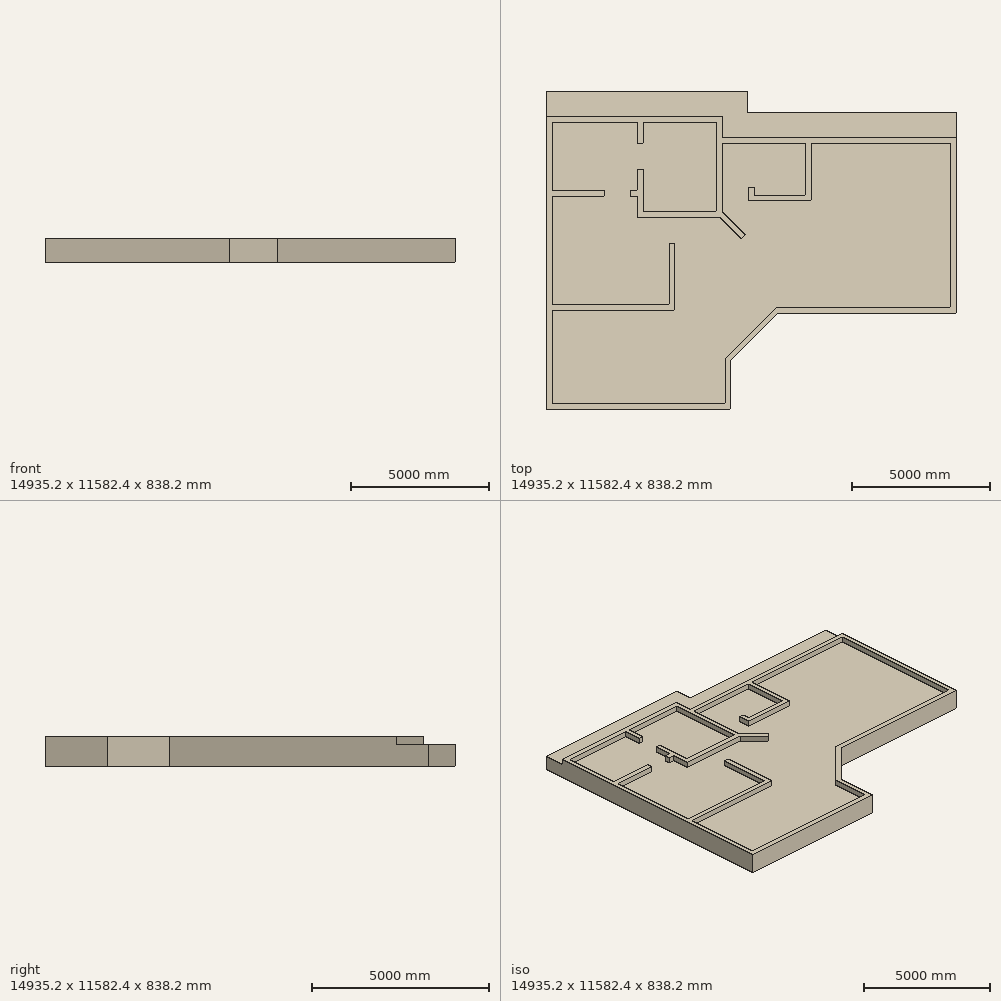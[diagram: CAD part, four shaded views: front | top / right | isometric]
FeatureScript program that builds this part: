
annotation { "Feature Type Name" : "Feature", "Feature Type Description" : "" }
export const myFeature = defineFeature(function(context is Context, id is Id, definition is map)
    precondition{}
    {
        {
            var Q0;
            Q0=qCreatedBy(makeId("Top.planeOp"),FACE);
            var sketch = newSketch(context, id + "F0", { "sketchPlane" : qUnion([Q0])});
            skLineSegment(sketch, "E0.bottom", {"start": v(0, 0) * mm, "end": v(14935.2, 0) * mm});
            skLineSegment(sketch, "E0.top", {"start": v(0, 11582.4) * mm, "end": v(7315.2, 11582.4) * mm});
            skLineSegment(sketch, "E0.left", {"start": v(0, 0) * mm, "end": v(0, 11582.4) * mm});
            skLineSegment(sketch, "E0.right", {"start": v(14935.2, 0) * mm, "end": v(14935.2, 10820.4) * mm});
            skLineSegment(sketch, "E1", {"start": v(14935.2, 10820.4) * mm, "end": v(7315.2, 10820.4) * mm});
            skLineSegment(sketch, "E2", {"start": v(7315.2, 10820.4) * mm, "end": v(7315.2, 11582.4) * mm});
            skLineSegment(sketch, "E3", {"start": v(6705.6, 0) * mm, "end": v(6705.6, 3505.2) * mm});
            skLineSegment(sketch, "E4", {"start": v(6705.6, 3505.2) * mm, "end": v(14935.2, 3505.2) * mm});
            skLineSegment(sketch, "E5", {"start": v(6705.6, 1752.6) * mm, "end": v(8458.2, 3505.2) * mm});
            skLineSegment(sketch, "E6", {"start": v(6705.6, 1752.6) * mm, "end": v(14935.2, 1752.6) * mm, "construction": true});
            skSolve(sketch);
        }
        {
            var Q0;
            Q0=makeQuery(id+"F0.imprint","IMPRINT",FACE,{"disambiguationData":[TD([[makeQuery(id+"F0.imprint","IMPRINT",EDGE,{"derivedFrom":sQuery(id+"F0.wireOp",EDGE,"E0.top")}),-1.0]])]});
            var Q1;
            {var subQ3=sQuery(id+"F0.wireOp",EDGE,"E5");Q1=makeQuery(id+"F0.imprint","IMPRINT",FACE,{"disambiguationData":[TD([[makeQuery(id+"F0.imprint","IMPRINT",EDGE,{"derivedFrom":subQ3}),1.0]])]});}
            extrude(context, id + "F1", {"entities" : qUnion([Q0, Q1]), "depth" : 609.6 * mm, "offsetDistance" : 25.4 * mm});
        }
        {
            var Q0;
            Q0=makeQuery(id+"F1.opExtrude","CAP_FACE",FACE,{"disambiguationData":[OSD([sQuery(id+"F0.wireOp",EDGE,"E0.bottom"),sQuery(id+"F0.wireOp",EDGE,"E0.top"),sQuery(id+"F0.wireOp",EDGE,"E0.left"),sQuery(id+"F0.wireOp",EDGE,"E0.right"),sQuery(id+"F0.wireOp",EDGE,"E1"),sQuery(id+"F0.wireOp",EDGE,"E2"),sQuery(id+"F0.wireOp",EDGE,"E3"),sQuery(id+"F0.wireOp",EDGE,"E4"),sQuery(id+"F0.wireOp",EDGE,"E5")])],"isStart":false});
            var sketch = newSketch(context, id + "F2", { "sketchPlane" : qUnion([Q0])});
            skLineSegment(sketch, "E7", {"start": v(0, 10668) * mm, "end": v(6400.8, 10668) * mm});
            skLineSegment(sketch, "E8", {"start": v(6400.8, 10668) * mm, "end": v(6400.8, 9906) * mm});
            skLineSegment(sketch, "E9", {"start": v(6400.8, 9906) * mm, "end": v(14935.2, 9906) * mm});
            skLineSegment(sketch, "E10", {"start": v(0, 10668) * mm, "end": v(0, 0) * mm});
            skLineSegment(sketch, "E11", {"start": v(0, 0) * mm, "end": v(6705.6, 0) * mm});
            skLineSegment(sketch, "E12", {"start": v(6705.6, 0) * mm, "end": v(6705.6, 1752.6) * mm});
            skLineSegment(sketch, "E13", {"start": v(6705.6, 1752.6) * mm, "end": v(8458.2, 3505.2) * mm});
            skLineSegment(sketch, "E14", {"start": v(8458.2, 3505.2) * mm, "end": v(14935.2, 3505.2) * mm});
            skLineSegment(sketch, "E15", {"start": v(14935.2, 3505.2) * mm, "end": v(14935.2, 9906) * mm});
            skLineSegment(sketch, "E16", {"start": v(203.2, 10464.8) * mm, "end": v(3327.4, 10464.8) * mm});
            skLineSegment(sketch, "E17", {"start": v(6400.8, 9702.8) * mm, "end": v(9448.8, 9702.8) * mm});
            skLineSegment(sketch, "E18", {"start": v(14732, 9702.8) * mm, "end": v(14732, 3708.4) * mm});
            skLineSegment(sketch, "E19", {"start": v(6502.4, 1836.77) * mm, "end": v(6502.4, 203.2) * mm});
            skLineSegment(sketch, "E20", {"start": v(6502.4, 203.2) * mm, "end": v(203.2, 203.2) * mm});
            skLineSegment(sketch, "E21", {"start": v(203.2, 203.2) * mm, "end": v(203.2, 3606.8) * mm});
            skLineSegment(sketch, "E22", {"start": v(14732, 3708.4) * mm, "end": v(8374.03, 3708.4) * mm});
            skLineSegment(sketch, "E23", {"start": v(8374.03, 3708.4) * mm, "end": v(6502.4, 1836.77) * mm});
            skLineSegment(sketch, "E24", {"start": v(6197.6, 7213.6) * mm, "end": v(3530.6, 7213.6) * mm});
            skLineSegment(sketch, "E25", {"start": v(6400.8, 7194.8) * mm, "end": v(6400.8, 9702.8) * mm});
            skLineSegment(sketch, "E26", {"start": v(3327.4, 7010.4) * mm, "end": v(3327.4, 7772.4) * mm});
            skLineSegment(sketch, "E27", {"start": v(3530.6, 10464.8) * mm, "end": v(3530.6, 9702.8) * mm});
            skLineSegment(sketch, "E28", {"start": v(3327.4, 9702.8) * mm, "end": v(3530.6, 9702.8) * mm});
            skLineSegment(sketch, "E29", {"start": v(3327.4, 8737.6) * mm, "end": v(3530.6, 8737.6) * mm});
            skLineSegment(sketch, "E30.trimOffspring", {"start": v(3530.6, 10464.8) * mm, "end": v(6197.6, 10464.8) * mm});
            skLineSegment(sketch, "E31.trimOffspring", {"start": v(3327.4, 9702.8) * mm, "end": v(3327.4, 10464.8) * mm});
            skLineSegment(sketch, "E32.trimOffspring", {"start": v(3530.6, 8737.6) * mm, "end": v(3530.6, 7213.6) * mm});
            skLineSegment(sketch, "E33.trimOffspring", {"start": v(203.2, 7416.8) * mm, "end": v(203.2, 7772.4) * mm});
            skLineSegment(sketch, "E34", {"start": v(3327.4, 7975.6) * mm, "end": v(3073.4, 7975.6) * mm});
            skLineSegment(sketch, "E35", {"start": v(203.2, 7772.4) * mm, "end": v(2108.2, 7772.4) * mm});
            skLineSegment(sketch, "E36", {"start": v(2108.2, 7975.6) * mm, "end": v(2108.2, 7772.4) * mm});
            skPoint(sketch, "E36.endSnap0", {"position": v(1765.3, 7772.4) * mm});
            skLineSegment(sketch, "E37.trimOffspring", {"start": v(203.2, 7975.6) * mm, "end": v(203.2, 10464.8) * mm});
            skLineSegment(sketch, "E38", {"start": v(3073.4, 7975.6) * mm, "end": v(3073.4, 7772.4) * mm});
            skLineSegment(sketch, "E39.trimOffspring", {"start": v(2108.2, 7975.6) * mm, "end": v(203.2, 7975.6) * mm});
            skLineSegment(sketch, "E40.trimOffspring", {"start": v(3073.4, 7772.4) * mm, "end": v(3327.4, 7772.4) * mm});
            skLineSegment(sketch, "E41.trimOffspring", {"start": v(3327.4, 7975.6) * mm, "end": v(3327.4, 8737.6) * mm});
            skLineSegment(sketch, "E42", {"start": v(9448.8, 9702.8) * mm, "end": v(9448.8, 7797.8) * mm});
            skLineSegment(sketch, "E43", {"start": v(9652, 7594.6) * mm, "end": v(9652, 9702.8) * mm});
            skLineSegment(sketch, "E44", {"start": v(9652, 7594.6) * mm, "end": v(7366, 7594.6) * mm});
            skLineSegment(sketch, "E45", {"start": v(7366, 7594.6) * mm, "end": v(7366, 8102.6) * mm});
            skLineSegment(sketch, "E46", {"start": v(7569.2, 8102.6) * mm, "end": v(7569.2, 7797.8) * mm});
            skPoint(sketch, "E47.orphan", {"position": v(9652, 7797.8) * mm});
            skLineSegment(sketch, "E48", {"start": v(9448.8, 7797.8) * mm, "end": v(7569.2, 7797.8) * mm});
            skLineSegment(sketch, "E49", {"start": v(7366, 8102.6) * mm, "end": v(7569.2, 8102.6) * mm});
            skLineSegment(sketch, "E50.trimOffspring", {"start": v(9652, 9702.8) * mm, "end": v(14732, 9702.8) * mm});
            skLineSegment(sketch, "E51", {"start": v(6197.6, 7213.6) * mm, "end": v(6197.6, 10464.8) * mm});
            skLineSegment(sketch, "E52", {"start": v(3327.4, 7010.4) * mm, "end": v(6297.83, 7010.4) * mm});
            skLineSegment(sketch, "E53", {"start": v(203.2, 3810) * mm, "end": v(4470.4, 3810) * mm});
            skLineSegment(sketch, "E54", {"start": v(4470.4, 3810) * mm, "end": v(4470.4, 6045.2) * mm});
            skLineSegment(sketch, "E55", {"start": v(203.2, 3606.8) * mm, "end": v(4673.6, 3606.8) * mm});
            skLineSegment(sketch, "E56", {"start": v(4673.6, 3606.8) * mm, "end": v(4673.6, 6045.2) * mm});
            skLineSegment(sketch, "E57", {"start": v(4470.4, 6045.2) * mm, "end": v(4673.6, 6045.2) * mm});
            skPoint(sketch, "E58.orphan", {"position": v(4673.6, 7010.4) * mm});
            skLineSegment(sketch, "E59.trimOffspring", {"start": v(203.2, 3810) * mm, "end": v(203.2, 7416.8) * mm});
            skLineSegment(sketch, "E60", {"start": v(7106.06, 6202.18) * mm, "end": v(7249.74, 6345.86) * mm});
            skLineSegment(sketch, "E61", {"start": v(7249.74, 6345.86) * mm, "end": v(6400.8, 7194.8) * mm});
            skLineSegment(sketch, "E62", {"start": v(7106.06, 6202.18) * mm, "end": v(6297.83, 7010.4) * mm});
            skPoint(sketch, "E63.orphan", {"position": v(6400.8, 7010.4) * mm});
            skSolve(sketch);
        }
        {
            var Q0;
            Q0 = qSketchRegion(id + "F2", true);
            extrude(context, id + "F3", {"entities" : qUnion([Q0]), "operationType" : NewBodyOperationType.ADD, "depth" : 228.6 * mm, "offsetDistance" : 25.4 * mm});
        }
    });
